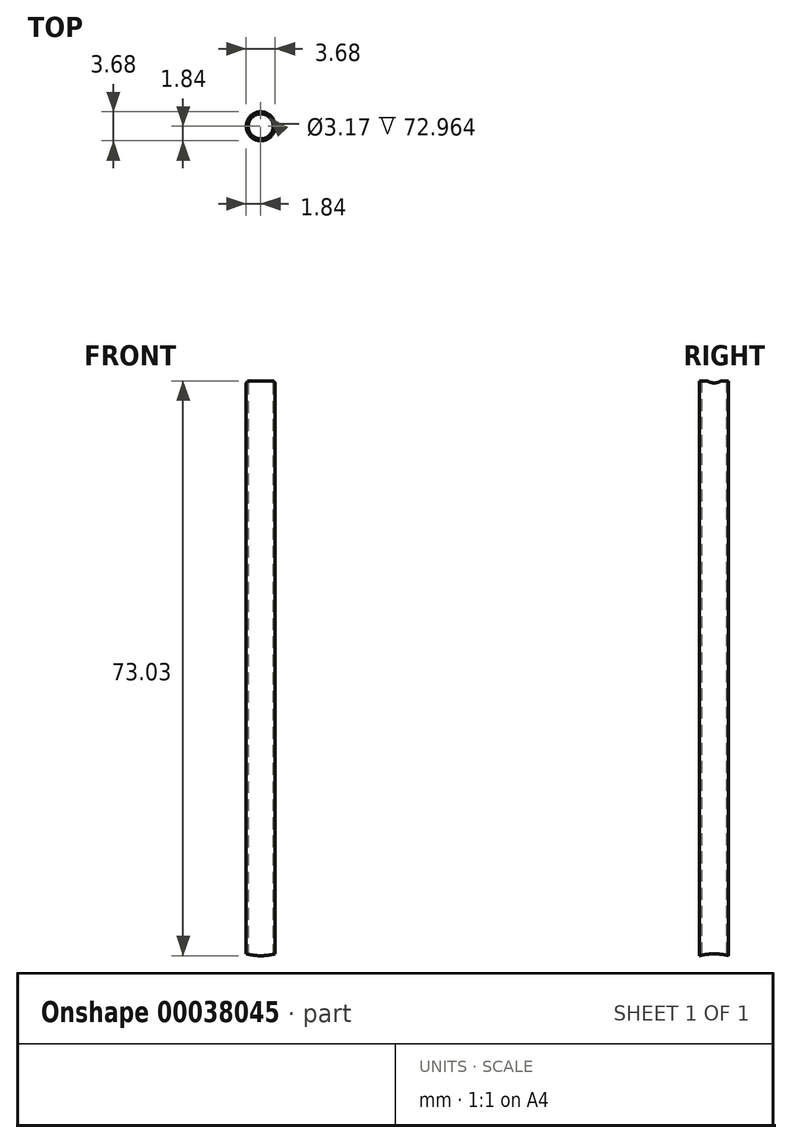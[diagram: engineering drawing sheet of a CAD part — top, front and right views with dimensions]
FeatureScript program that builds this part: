
annotation { "Feature Type Name" : "Feature", "Feature Type Description" : "" }
export const myFeature = defineFeature(function(context is Context, id is Id, definition is map)
    precondition{}
    {
        {
            var Q0;
            Q0=qCreatedBy(makeId("Top.planeOp"),FACE);
            var sketch = newSketch(context, id + "F0", { "sketchPlane" : qUnion([Q0])});
            skLineSegment(sketch, "E0.rect.bottom", {"start": v(1.84, -1.84) * mm, "end": v(-1.84, -1.84) * mm});
            skLineSegment(sketch, "E0.rect.top", {"start": v(1.84, 1.84) * mm, "end": v(-1.84, 1.84) * mm});
            skLineSegment(sketch, "E0.rect.left", {"start": v(1.84, -1.84) * mm, "end": v(1.84, 1.84) * mm});
            skLineSegment(sketch, "E0.rect.right", {"start": v(-1.84, -1.84) * mm, "end": v(-1.84, 1.84) * mm});
            skPoint(sketch, "E0.rect.middle", {"position": v(0, 0) * mm});
            skCircle(sketch, "E1", {"center": v(0, 0) * mm, "radius": 1.59 * mm});
            skSolve(sketch);
        }
        {
            var Q0;
            Q0=qSketchRegion(id+"F0",true);
            extrude(context, id + "F1", {"entities" : qUnion([Q0]), "depth" : 73.02 * mm});
        }
        {
            var Q0;
            Q0=makeQuery(id+"F1.opExtrude","SWEPT_FACE",FACE,{"disambiguationData":[OSD([sQuery(id+"F0.wireOp",EDGE,"E0.rect.left")])]});
            var sketch = newSketch(context, id + "F2", { "sketchPlane" : qUnion([Q0])});
            skArc(sketch, "E2", {"start": v(-0.86, 73.03) * mm, "mid": v(0, 72.77) * mm, "end": v(0.86, 73.03) * mm});
            skLineSegment(sketch, "E3", {"start": v(0, 73.03) * mm, "end": v(0, 74.36) * mm, "construction": true});
            skPoint(sketch, "E3.endSnap0", {"position": v(0, 73.03) * mm});
            skLineSegment(sketch, "E4", {"start": v(0, 73.03) * mm, "end": v(0, 72.77) * mm, "construction": true});
            skLineSegment(sketch, "E5", {"start": v(-0.86, 73.03) * mm, "end": v(0.86, 73.03) * mm});
            skLineSegment(sketch, "E6", {"start": v(0, 0) * mm, "end": v(0, -6.9) * mm});
            skArc(sketch, "E7", {"start": v(1.84, 0) * mm, "mid": v(0, 0.24) * mm, "end": v(-1.84, 0) * mm});
            skLineSegment(sketch, "E8", {"start": v(-1.84, 0) * mm, "end": v(1.84, 0) * mm});
            skSolve(sketch);
        }
        {
            var Q0;
            Q0=qSketchRegion(id+"F2",true);
            var Q1;
            Q1=makeQuery(id+"F1.opExtrude","SWEPT_FACE",FACE,{"disambiguationData":[OSD([sQuery(id+"F0.wireOp",EDGE,"E0.rect.right")])]});
            extrude(context, id + "F3", {"entities" : qUnion([Q0]), "operationType" : NewBodyOperationType.REMOVE, "endBound" : BoundingType.UP_TO_SURFACE, "oppositeDirection" : true, "endBoundEntityFace" : qUnion([Q1]), "depth" : 25.4 * mm});
        }
        {
            var Q0;
            Q0=makeQuery(id+"F1.opExtrude","SWEPT_EDGE",EDGE,{"disambiguationData":[OSD([sQuery(id+"F0.wireOp",EDGE,"E0.rect.bottom"),sQuery(id+"F0.wireOp",EDGE,"E0.rect.right")])]});
            var Q1;
            Q1=makeQuery(id+"F1.opExtrude","SWEPT_EDGE",EDGE,{"disambiguationData":[OSD([sQuery(id+"F0.wireOp",EDGE,"E0.rect.bottom"),sQuery(id+"F0.wireOp",EDGE,"E0.rect.left")])]});
            var Q2;
            Q2=makeQuery(id+"F1.opExtrude","SWEPT_EDGE",EDGE,{"disambiguationData":[OSD([sQuery(id+"F0.wireOp",EDGE,"E0.rect.top"),sQuery(id+"F0.wireOp",EDGE,"E0.rect.right")])]});
            var Q3;
            Q3=makeQuery(id+"F1.opExtrude","SWEPT_EDGE",EDGE,{"disambiguationData":[OSD([sQuery(id+"F0.wireOp",EDGE,"E0.rect.top"),sQuery(id+"F0.wireOp",EDGE,"E0.rect.left")])]});
            fillet(context, id + "F4", {"entities" : qUnion([Q0, Q1, Q2, Q3]), "radius" : 1.84 * mm, "tangentPropagation" : true, "allowEdgeOverflow" : false});
        }
    });
